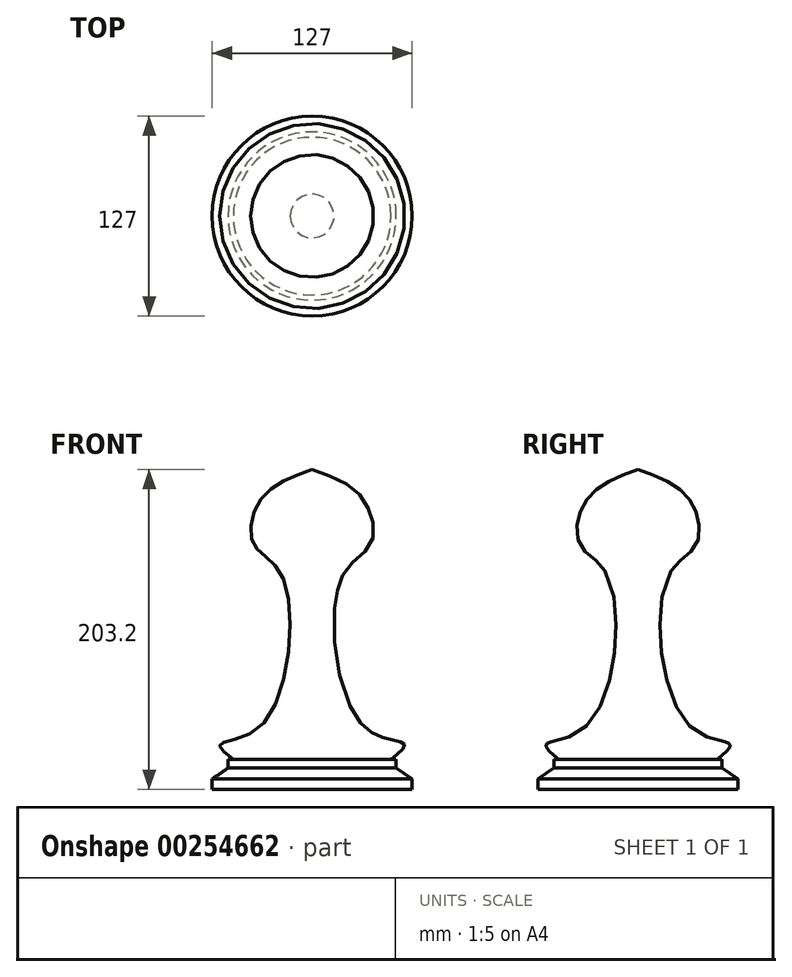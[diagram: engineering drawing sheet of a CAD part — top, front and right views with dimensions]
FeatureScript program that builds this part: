
annotation { "Feature Type Name" : "Feature", "Feature Type Description" : "" }
export const myFeature = defineFeature(function(context is Context, id is Id, definition is map)
    precondition{}
    {
        {
            var Q0;
            Q0=qCreatedBy(makeId("Front.planeOp"),FACE);
            var sketch = newSketch(context, id + "F0", { "sketchPlane" : qUnion([Q0])});
            skLineSegment(sketch, "E0", {"start": v(0, 118.37) * mm, "end": v(0, -84.83) * mm, "construction": true});
            skLineSegment(sketch, "E1", {"start": v(0, -84.83) * mm, "end": v(-63.5, -84.83) * mm});
            skLineSegment(sketch, "E2", {"start": v(-63.5, -84.83) * mm, "end": v(-63.5, -78.2) * mm});
            skLineSegment(sketch, "E3", {"start": v(-63.5, -78.2) * mm, "end": v(-53.4, -71.2) * mm});
            skLineSegment(sketch, "E4", {"start": v(-53.4, -71.2) * mm, "end": v(-53.4, -65.71) * mm});
            skLineSegment(sketch, "E5", {"start": v(-53.4, -65.71) * mm, "end": v(-50.09, -65.71) * mm});
            skFitSpline(sketch, "E6", {"points": [v(-50.09, -65.71) * mm, v(-58.64, -56.26) * mm, v(-32.59, -44.51) * mm, v(-18.8, 50.01) * mm, v(-37.19, 70.96) * mm, v(-32.08, 100.08) * mm, v(0, 118.37) * mm], "startDerivative": vector(-142.2, 111.7) * mm, "endDerivative": vector(217.33, 75.3) * mm});
            skSolve(sketch);
        }
        {
            var Q0;
            Q0=sQuery(id+"F0.wireOp",EDGE,"E1");
            var Q1;
            Q1=sQuery(id+"F0.wireOp",EDGE,"E6");
            var Q2;
            Q2=sQuery(id+"F0.wireOp",EDGE,"E3");
            var Q3;
            Q3=sQuery(id+"F0.wireOp",EDGE,"E4");
            var Q4;
            Q4=sQuery(id+"F0.wireOp",EDGE,"E2");
            var Q5;
            Q5=sQuery(id+"F0.wireOp",EDGE,"E0");
            revolve(context, id + "F1", {"bodyType" : ToolBodyType.SURFACE, "surfaceEntities" : qUnion([Q0, Q1, Q2, Q3, Q4]), "axis" : qUnion([Q5]), "revolveType" : RevolveType.FULL});
        }
    });
